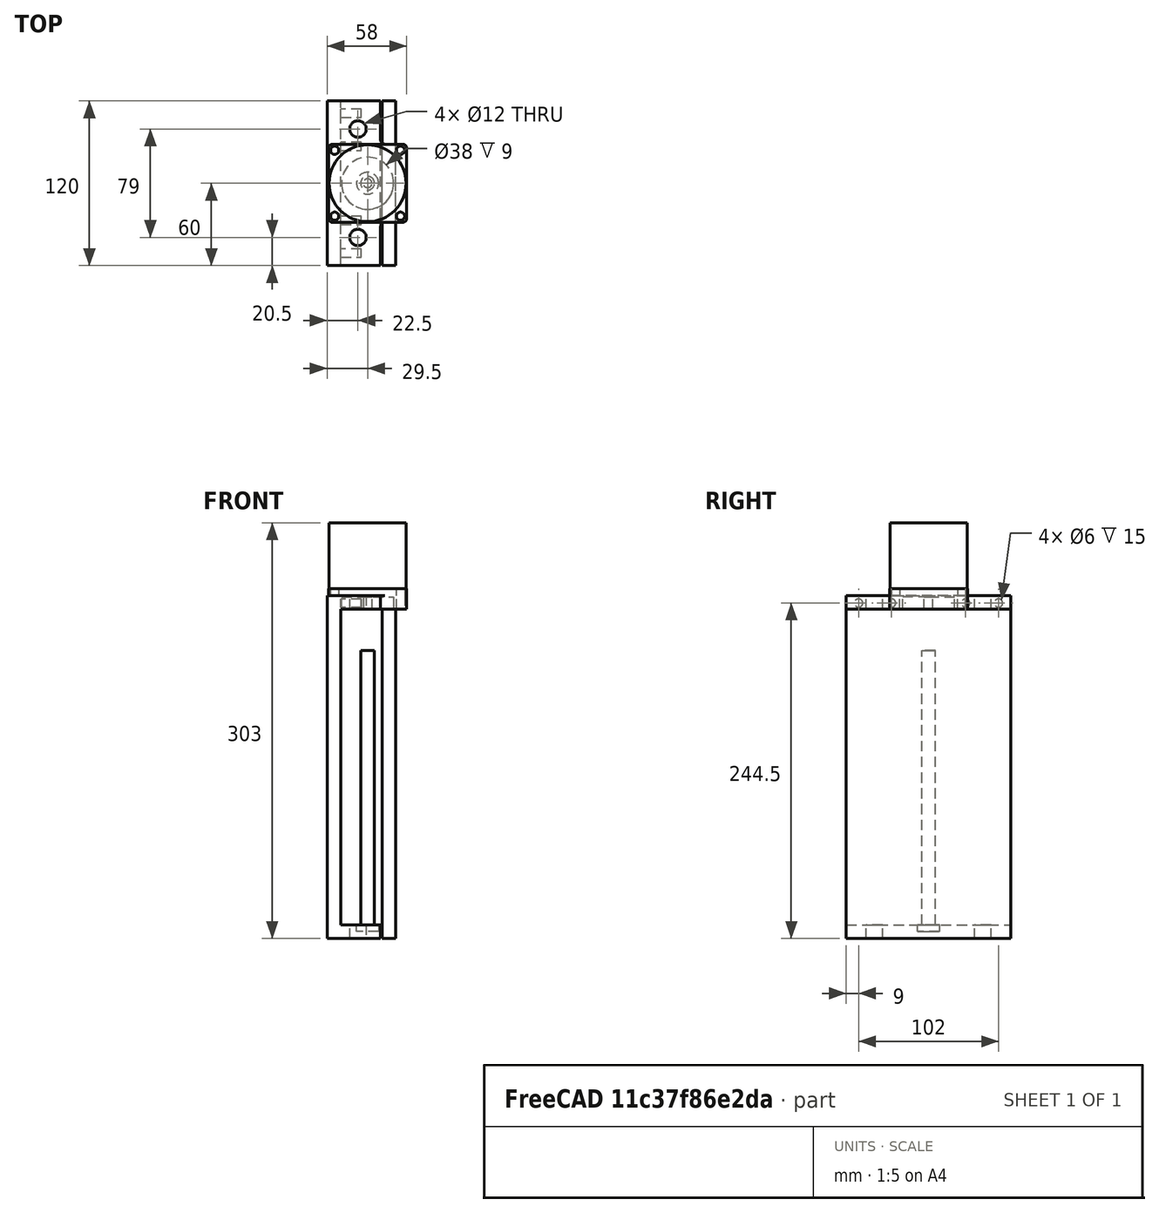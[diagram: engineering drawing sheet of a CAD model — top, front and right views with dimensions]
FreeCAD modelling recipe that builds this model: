
FCSTD DOCUMENT
Label: Z
objects: Part::MultiFuse×4, PartDesign::Pocket×3, Part::Box×2, Part::Cylinder×1
note: 13 computed .brp shape members not serialized (recipe doc carries the construction recipe); baked Part::Feature solids carry a one-line shape summary decoded from their .brp

FEATURE [Part::Box] Box
  Height = 250
  Length = 10
  Width = 120
FEATURE [PartDesign::Pocket] Pocket  label="Z_B"
  Length = 5
  Placement = pos=(10,0,0) rot=(0,0,1;0rad)
  Type = 0
FEATURE [PartDesign::Pocket] Pocket001  label="Z_T"
  Length = 5
  Placement = pos=(10,0,250) rot=(0,0,1;0rad)
  Type = 1
FEATURE [PartDesign::Pocket] Pocket002  label="A_M"
  Length = 5
  Placement = pos=(1,31.5,255) rot=(-1,0,0;1.5708rad)
  Type = 1
FEATURE [Part::Cylinder] Cylinder
  Angle = 360
  Height = 200
  Placement = pos=(29.5,60,10) rot=(0,0,1;0rad)
  Radius = 5
FEATURE [Part::Box] Box001
  Height = 240
  Length = 10
  Placement = pos=(40,0,0) rot=(0,0,1;0rad)
  Width = 120
FEATURE [Part::MultiFuse] Fusion
  Shapes = -> [Pocket002,Cylinder]
FEATURE [Part::MultiFuse] Fusion001
  Shapes = -> [Pocket001,Pocket]
FEATURE [Part::MultiFuse] Fusion002
  Shapes = -> [Box,Fusion]
FEATURE [Part::MultiFuse] Fusion003
  Shapes = -> [Fusion001,Fusion002]
